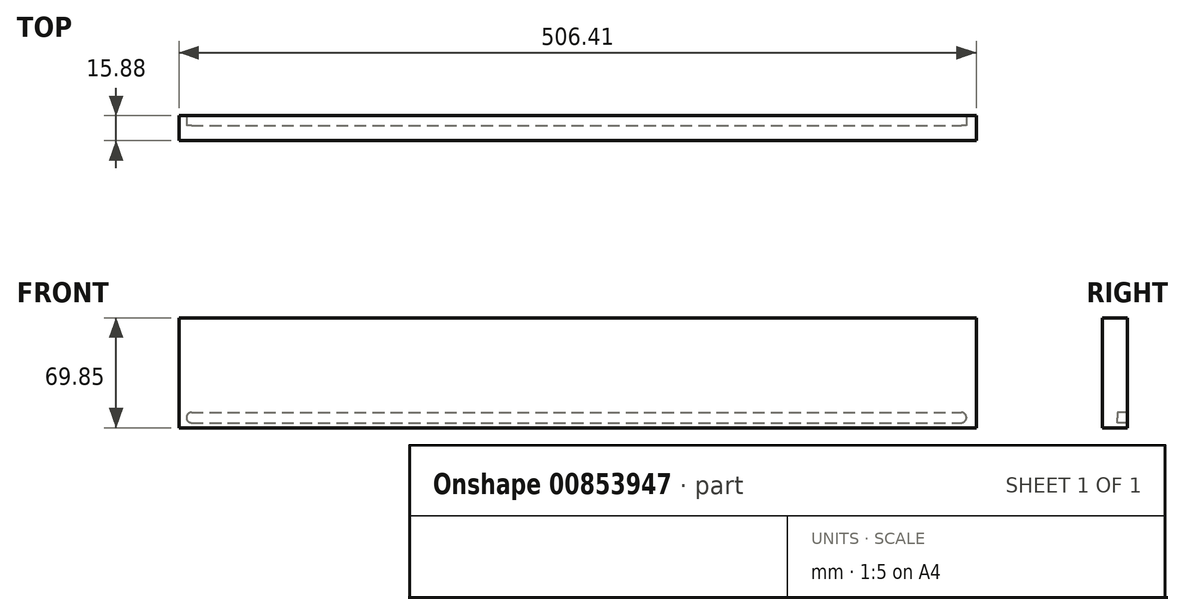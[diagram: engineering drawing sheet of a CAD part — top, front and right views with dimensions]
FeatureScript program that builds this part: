
annotation { "Feature Type Name" : "Feature", "Feature Type Description" : "" }
export const myFeature = defineFeature(function(context is Context, id is Id, definition is map)
    precondition{}
    {
        {
            var Q0;
            Q0=qCreatedBy(makeId("Front.planeOp"),FACE);
            var sketch = newSketch(context, id + "F0", { "sketchPlane" : qUnion([Q0])});
            skLineSegment(sketch, "E0.bottom", {"start": v(0, 69.85) * mm, "end": v(506.41, 69.85) * mm});
            skLineSegment(sketch, "E0.top", {"start": v(0, 0) * mm, "end": v(506.41, 0) * mm});
            skLineSegment(sketch, "E0.left", {"start": v(0, 69.85) * mm, "end": v(0, 0) * mm});
            skLineSegment(sketch, "E0.right", {"start": v(506.41, 69.85) * mm, "end": v(506.41, 0) * mm});
            skSolve(sketch);
        }
        {
            var Q0;
            Q0=makeQuery(id+"F0.imprint","IMPRINT",FACE,{"disambiguationData":[TD([[makeQuery(id+"F0.imprint","IMPRINT",EDGE,{"derivedFrom":sQuery(id+"F0.wireOp",EDGE,"E0.bottom")}),-1.0]])]});
            extrude(context, id + "F1", {"entities" : qUnion([Q0]), "oppositeDirection" : true, "depth" : 15.88 * mm, "offsetDistance" : 25.4 * mm});
        }
        {
            var Q0;
            Q0=makeQuery(id+"F1.opExtrude","SWEPT_FACE",FACE,{"disambiguationData":[OSD([sQuery(id+"F0.wireOp",EDGE,"E0.right")])]});
            var sketch = newSketch(context, id + "F2", { "sketchPlane" : qUnion([Q0])});
            skLineSegment(sketch, "E1.bottom", {"start": v(22.23, 9.78) * mm, "end": v(9.53, 9.78) * mm});
            skLineSegment(sketch, "E1.top", {"start": v(22.23, 3.17) * mm, "end": v(9.53, 3.17) * mm});
            skLineSegment(sketch, "E1.left", {"start": v(22.23, 9.78) * mm, "end": v(22.23, 3.17) * mm});
            skLineSegment(sketch, "E1.right", {"start": v(9.53, 9.78) * mm, "end": v(9.53, 3.17) * mm});
            skSolve(sketch);
        }
        {
            var Q0;
            {var subQ0=sQuery(id+"F2.wireOp",EDGE,"E1.right");Q0=makeQuery(id+"F2.imprint","IMPRINT",FACE,{"disambiguationData":[TD([[makeQuery(id+"F2.imprint","IMPRINT",EDGE,{"derivedFrom":subQ0}),1.0]])]});}
            extrude(context, id + "F3", {"entities" : qUnion([Q0]), "operationType" : NewBodyOperationType.REMOVE, "oppositeDirection" : true, "depth" : 501.65 * mm, "offsetDistance" : 25.4 * mm, "hasSecondDirection" : true, "secondDirectionOppositeDirection" : false, "secondDirectionDepth" : -6.35 * mm});
        }
        {
            var Q0;
            Q0=makeQuery(id+"F3.boolean.opBoolean","COPY",EDGE,{"derivedFrom":makeQuery(id+"F3.opExtrude","CAP_EDGE",EDGE,{"disambiguationData":[OSD([sQuery(id+"F2.wireOp",EDGE,"E1.bottom")])],"isStart":true})});
            var Q1;
            Q1=makeQuery(id+"F3.boolean.opBoolean","COPY",EDGE,{"derivedFrom":makeQuery(id+"F3.opExtrude","CAP_EDGE",EDGE,{"disambiguationData":[OSD([sQuery(id+"F2.wireOp",EDGE,"E1.top")])],"isStart":true})});
            var Q2;
            Q2=makeQuery(id+"F3.boolean.opBoolean","COPY",EDGE,{"derivedFrom":makeQuery(id+"F3.opExtrude","CAP_EDGE",EDGE,{"disambiguationData":[OSD([sQuery(id+"F2.wireOp",EDGE,"E1.top")])],"isStart":false})});
            var Q3;
            Q3=makeQuery(id+"F3.boolean.opBoolean","COPY",EDGE,{"derivedFrom":makeQuery(id+"F3.opExtrude","CAP_EDGE",EDGE,{"disambiguationData":[OSD([sQuery(id+"F2.wireOp",EDGE,"E1.bottom")])],"isStart":false})});
            fillet(context, id + "F4", {"entities" : qUnion([Q0, Q1, Q2, Q3]), "radius" : 3.17 * mm, "tangentPropagation" : true, "allowEdgeOverflow" : false});
        }
    });
